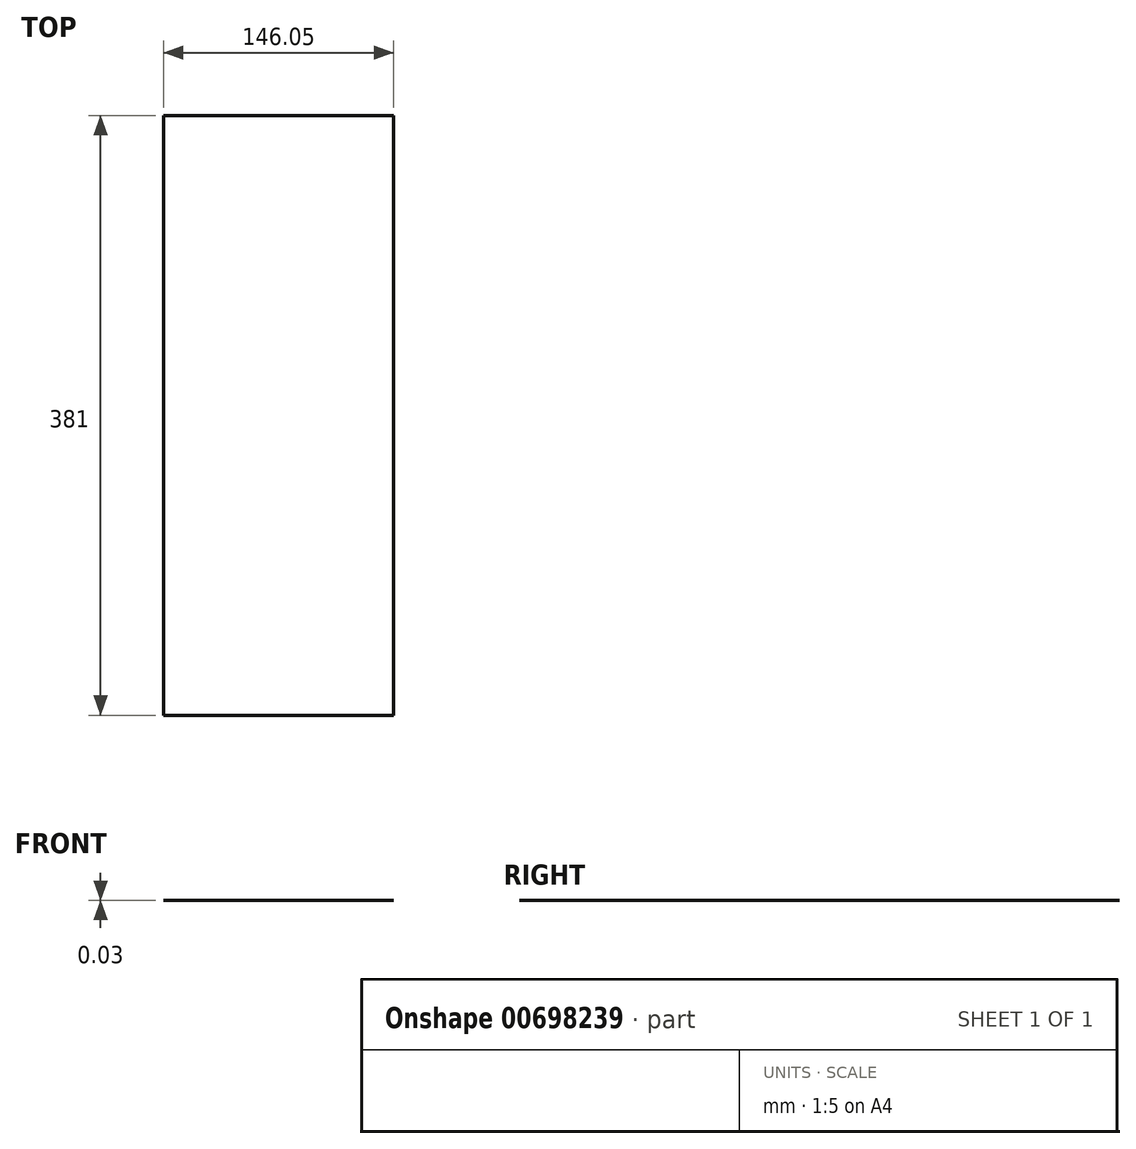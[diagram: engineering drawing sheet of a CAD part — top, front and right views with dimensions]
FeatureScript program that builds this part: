
annotation { "Feature Type Name" : "Feature", "Feature Type Description" : "" }
export const myFeature = defineFeature(function(context is Context, id is Id, definition is map)
    precondition{}
    {
        {
            var Q0;
            Q0=qCreatedBy(makeId("Top.planeOp"),FACE);
            var sketch = newSketch(context, id + "F0", { "sketchPlane" : qUnion([Q0])});
            skLineSegment(sketch, "E0", {"start": v(-72.38, 307.55) * mm, "end": v(-72.38, -73.45) * mm});
            skLineSegment(sketch, "E1", {"start": v(-72.38, -73.45) * mm, "end": v(73.67, -73.45) * mm});
            skLineSegment(sketch, "E2", {"start": v(73.67, -73.45) * mm, "end": v(73.67, 307.55) * mm});
            skLineSegment(sketch, "E3", {"start": v(73.67, 307.55) * mm, "end": v(-72.38, 307.55) * mm});
            skSolve(sketch);
        }
        {
            var Q0;
            Q0 = qSketchRegion(id + "F0", true);
            extrude(context, id + "F1", {"entities" : qUnion([Q0]), "depth" : 3 / 101.6 * mm, "offsetDistance" : 25.4 * mm});
        }
    });
